# Revit family: Bathtub-Stationary_Whirlpool-Whitehall-H-75-S-Series
name_source: partatom
category: Plumbing Fixtures
units: mm (PartAtom-declared; Revit-internal decimal feet)

## family parameters
Cut with Voids When Loaded = No
Host = Face
OmniClass Number = 23.45.05.14.21.17
OmniClass Title = Therapeutic Whirlpool Baths
Part Type = Normal
Room Calculation Point = No
Round Connector Dimension = Use Diameter
Shared = Yes

## types (3) — shared parameters
115VAC = Yes
230VAC = No
75 75 Gallons = Yes
AHC1  Adjustable High Chair with Casters = No
AHC2  Adjustable High Chair with Rubber Tips = No
ARS  Arm Rest Support = No
AS1  Adjustable Suspension Seat = No
Assembly Code = D2010510
CTS1  Combination Table with Side Seats = No
CW Connection = Yes
CWFU = 3
Default Elevation = 0"
Depth = 28"
Description = H-75-S 75 Gallon Stationary Whirlpool
Electrical Requirements = Amps:6.9/6.2 Hertz:50/60 Volts:115 GFI Receptable
Finish - Mobile Turbine = Plastic-Whitehall-Plastic Greyish
GAL. TO OVERFLOW = 75  Gallon
GFI Ground Fault Interrupter = No
H   Hi-Boy Series = Yes
HW Connection = Yes
HWFU = 3
Height = 33 1/2"
IAPMO Compliance = Certified per US & Canadian Medical Standards; UL 60601-1 & CSA C22.2 No. 601.1
Installation Type = Floor Mount
Length = 42"
Manufacturer = Whitehall
PCS   Pump Strainer Cover = No
Price = Prices may vary. Please consult Manufacturer Representative for most up-to-date price list.
Product Documentation Link = https://www.whitehallmfg.com
Product Page URL = https://whitehallrehabilitation.com
RHG   Rubber Hand Grips = No
S Stationary Whirlpool = Yes
SDO Separate Drain and Overflow Assembly = No
TTS1  Tank Top Seat = No
URL = https://whitehallrehabilitation.com
Vent Connection = No
WFU = 4
Waste Connection = Yes
Waste Connection Diameter = 2"
Waste Connection Radius = 1"
Width = 20"

## per-type parameters (varying)
| type | EG Enviro Glaze Color Powder Coating Specify Color | Finish | Material |
| H-75-S | No | Stainless Steel-Whitehall-Satin Finish | Stainless Steel-Whitehall-Satin Finish |
| H-75-S-EG07 | Yes | Stainless Steel-Whitehall-EG07-Black Color Enviro Glaze | Stainless Steel-Whitehall-EG07-Black Color Enviro Glaze |
| H-75-S-EG10 | Yes | Stainless Steel-Whitehall-EG10-White Enviro Glaze | Stainless Steel-Whitehall-EG10-White Enviro Glaze |

note: column(s) folded — value = type name in every type: Model

## geometry (parser evidence)
native form markers: Sweep x2
no freeform markers — native parametric forms only
